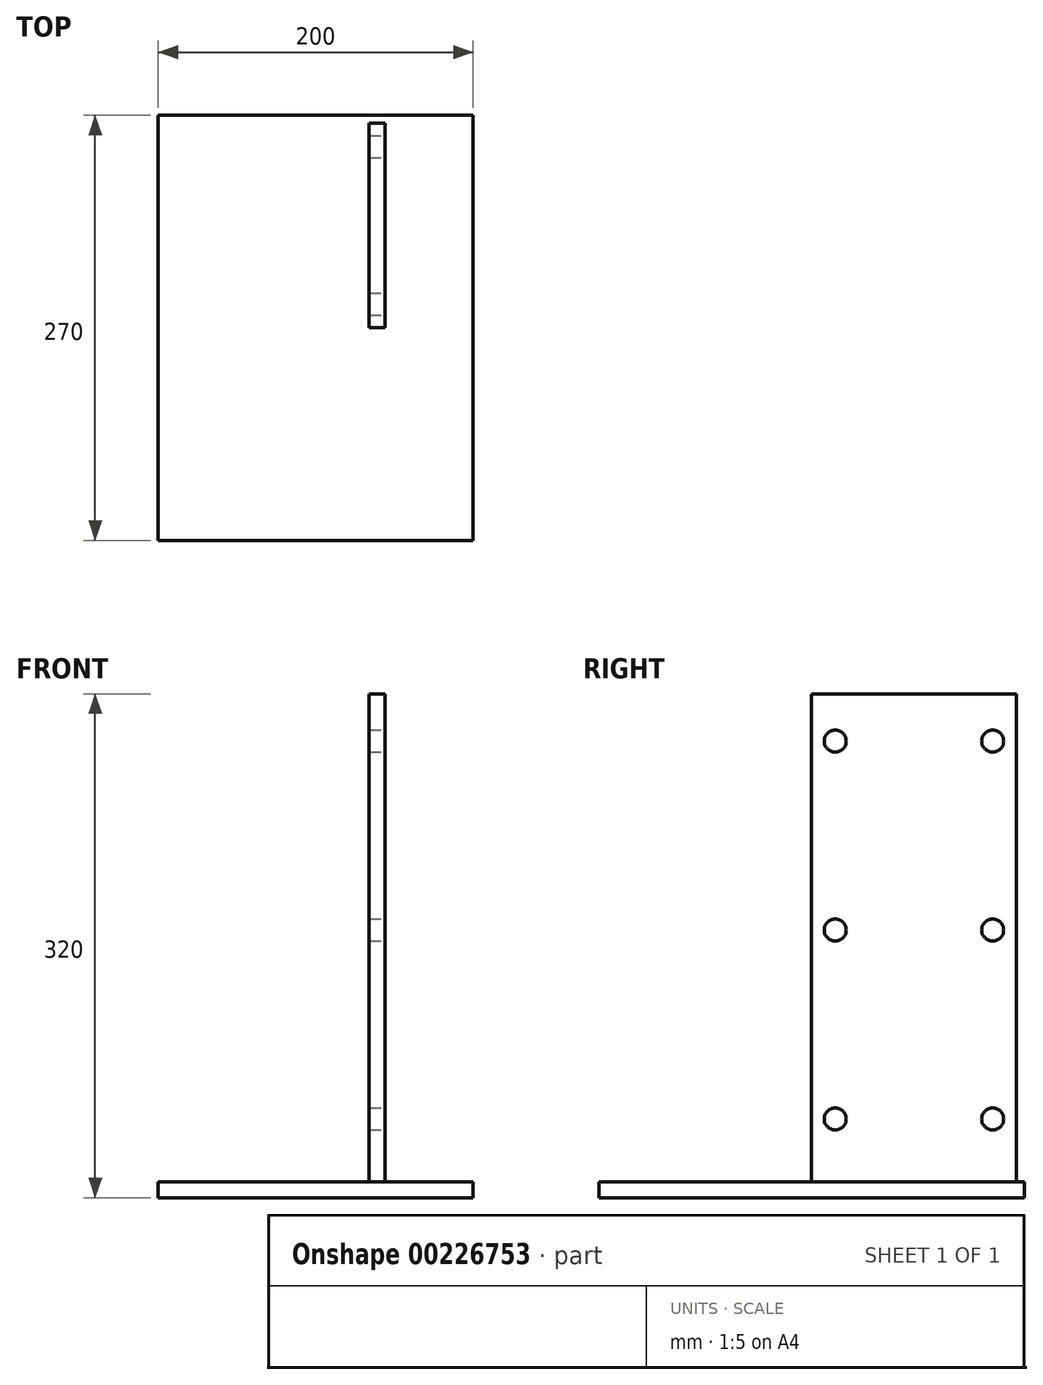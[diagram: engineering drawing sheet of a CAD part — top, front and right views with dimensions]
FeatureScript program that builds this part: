
annotation { "Feature Type Name" : "Feature", "Feature Type Description" : "" }
export const myFeature = defineFeature(function(context is Context, id is Id, definition is map)
    precondition{}
    {
        {
            var Q0;
            Q0=qCreatedBy(makeId("Top.planeOp"),FACE);
            var sketch = newSketch(context, id + "F0", { "sketchPlane" : qUnion([Q0])});
            skLineSegment(sketch, "E0.bottom", {"start": v(0, 0) * mm, "end": v(200, 0) * mm});
            skLineSegment(sketch, "E0.top", {"start": v(0, 270) * mm, "end": v(200, 270) * mm});
            skLineSegment(sketch, "E0.left", {"start": v(0, 0) * mm, "end": v(0, 270) * mm});
            skLineSegment(sketch, "E0.right", {"start": v(200, 0) * mm, "end": v(200, 270) * mm});
            skSolve(sketch);
        }
        {
            var Q0;
            Q0 = qSketchRegion(id + "F0", true);
            extrude(context, id + "F1", {"entities" : qUnion([Q0]), "depth" : 10 * mm});
        }
        {
            var Q0;
            Q0=makeQuery(id+"F1.opExtrude","CAP_FACE",FACE,{"disambiguationData":[OSD([sQuery(id+"F0.wireOp",EDGE,"E0.bottom"),sQuery(id+"F0.wireOp",EDGE,"E0.top"),sQuery(id+"F0.wireOp",EDGE,"E0.left"),sQuery(id+"F0.wireOp",EDGE,"E0.right")])],"isStart":false});
            var sketch = newSketch(context, id + "F2", { "sketchPlane" : qUnion([Q0])});
            skLineSegment(sketch, "E1.bottom", {"start": v(134, 265) * mm, "end": v(144, 265) * mm});
            skLineSegment(sketch, "E1.top", {"start": v(134, 135) * mm, "end": v(144, 135) * mm});
            skLineSegment(sketch, "E1.left", {"start": v(134, 265) * mm, "end": v(134, 135) * mm});
            skLineSegment(sketch, "E1.right", {"start": v(144, 265) * mm, "end": v(144, 135) * mm});
            skSolve(sketch);
        }
        {
            var Q0;
            Q0 = qSketchRegion(id + "F2", true);
            extrude(context, id + "F3", {"entities" : qUnion([Q0]), "operationType" : NewBodyOperationType.ADD, "depth" : 310 * mm});
        }
        {
            var Q0;
            Q0=makeQuery(id+"F3.opExtrude","SWEPT_FACE",FACE,{"disambiguationData":[OSD([sQuery(id+"F2.wireOp",EDGE,"E1.right")])]});
            var sketch = newSketch(context, id + "F4", { "sketchPlane" : qUnion([Q0])});
            skPoint(sketch, "E2", {"position": v(150, 50) * mm});
            skPoint(sketch, "E3", {"position": v(150, 170) * mm});
            skPoint(sketch, "E4", {"position": v(150, 290) * mm});
            skPoint(sketch, "E5.1.0.0", {"position": v(250, 290) * mm});
            skPoint(sketch, "E5.1.0.1", {"position": v(250, 170) * mm});
            skPoint(sketch, "E5.1.0.2", {"position": v(250, 50) * mm});
            skLineSegment(sketch, "E5.direction1", {"start": v(150, 290) * mm, "end": v(250, 290) * mm, "construction": true});
            skSolve(sketch);
        }
        {
            var Q0;
            Q0=sQuery(id+"F4.wireOp",VERTEX,"E4");
            var Q1;
            Q1=sQuery(id+"F4.wireOp",VERTEX,"E5.1.0.0");
            var Q2;
            Q2=sQuery(id+"F4.wireOp",VERTEX,"E5.1.0.1");
            var Q3;
            Q3=sQuery(id+"F4.wireOp",VERTEX,"E3");
            var Q4;
            Q4=sQuery(id+"F4.wireOp",VERTEX,"E2");
            var Q5;
            Q5=sQuery(id+"F4.wireOp",VERTEX,"E5.1.0.2");
            var Q6;
            Q6=makeQuery(id+"F1.opExtrude","SWEPT_BODY",BODY,{"disambiguationData":[OSD([sQuery(id+"F0.wireOp",EDGE,"E0.bottom"),sQuery(id+"F0.wireOp",EDGE,"E0.top"),sQuery(id+"F0.wireOp",EDGE,"E0.left"),sQuery(id+"F0.wireOp",EDGE,"E0.right")])]});
            hole(context, id + "F5", {"style" : HoleStyle.SIMPLE, "endStyle" : HoleEndStyle.THROUGH, "holeDiameter" : 14 * mm, "locations" : qUnion([Q0, Q1, Q2, Q3, Q4, Q5]), "scope" : qUnion([Q6]), "isTappedThrough" : true});
        }
    });
